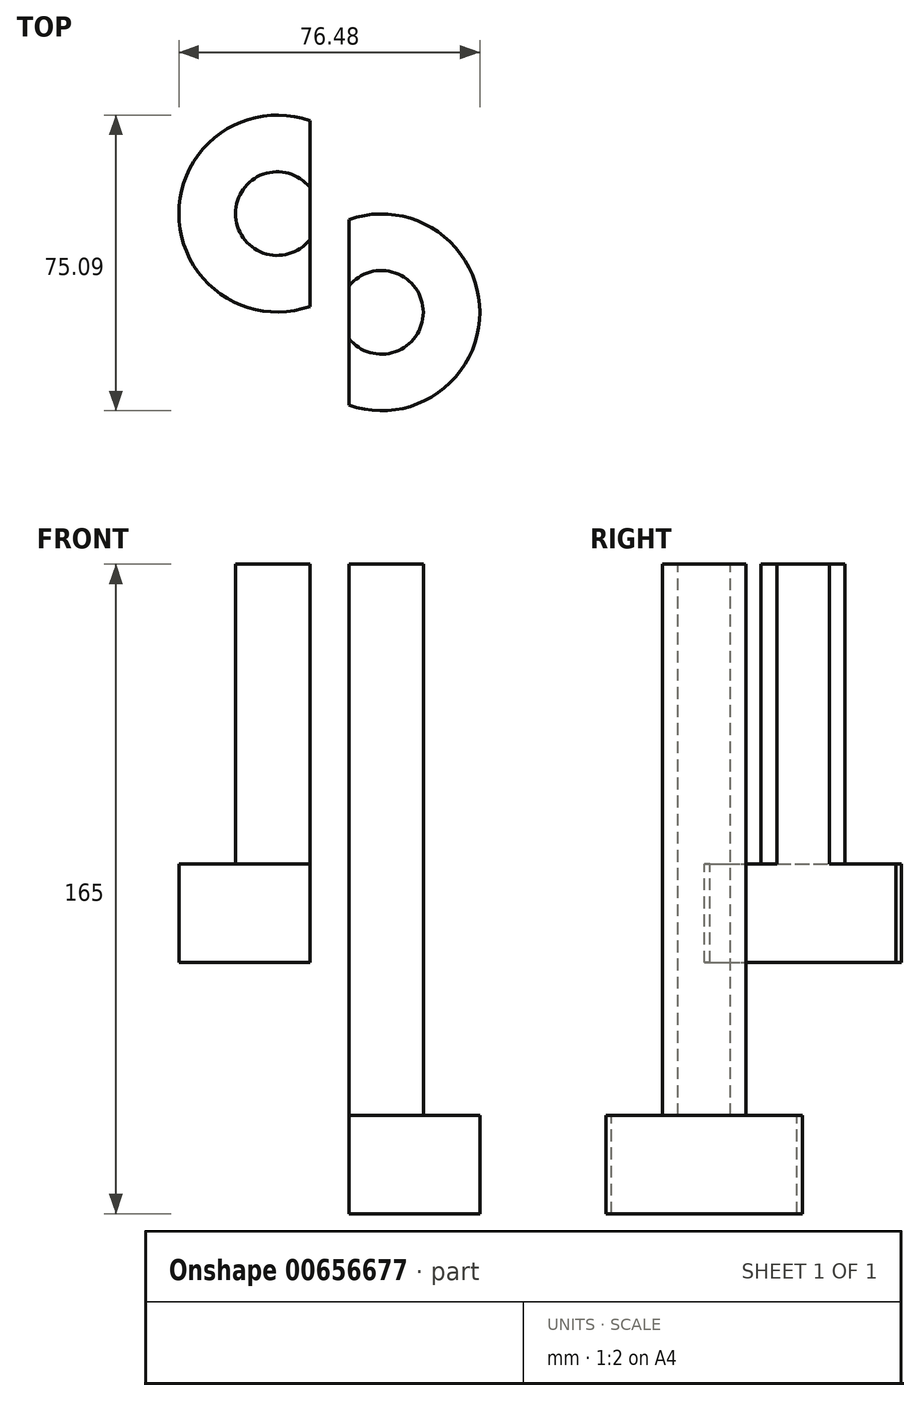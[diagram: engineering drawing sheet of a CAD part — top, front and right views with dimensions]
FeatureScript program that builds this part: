
annotation { "Feature Type Name" : "Feature", "Feature Type Description" : "" }
export const myFeature = defineFeature(function(context is Context, id is Id, definition is map)
    precondition{}
    {
        {
            var Q0;
            Q0=qCreatedBy(makeId("Top.planeOp"),FACE);
            var sketch = newSketch(context, id + "F0", { "sketchPlane" : qUnion([Q0])});
            skCircle(sketch, "E0", {"center": v(-17.72, 0) * mm, "radius": 10.62 * mm});
            skCircle(sketch, "E1", {"center": v(20.06, 0) * mm, "radius": 10.62 * mm});
            skLineSegment(sketch, "E2", {"start": v(-9.44, 6.66) * mm, "end": v(-9.44, -6.66) * mm});
            skLineSegment(sketch, "E3", {"start": v(11.78, 6.66) * mm, "end": v(11.78, -6.66) * mm});
            skPoint(sketch, "E4", {"position": v(-9.44, 0) * mm});
            skSolve(sketch);
        }
        {
            var Q0;
            {var subQ0=sQuery(id+"F0.wireOp",EDGE,"E2");Q0=makeQuery(id+"F0.imprint","IMPRINT",FACE,{"disambiguationData":[TD([[makeQuery(id+"F0.imprint","IMPRINT",EDGE,{"derivedFrom":subQ0}),-1.0]])]});}
            extrude(context, id + "F1", {"entities" : qUnion([Q0]), "depth" : 140 * mm, "offsetDistance" : 25 * mm});
        }
        {
            var Q0;
            {var subQ0=sQuery(id+"F0.wireOp",EDGE,"E3");Q0=makeQuery(id+"F0.imprint","IMPRINT",FACE,{"disambiguationData":[TD([[makeQuery(id+"F0.imprint","IMPRINT",EDGE,{"derivedFrom":subQ0}),1.0]])]});}
            extrude(context, id + "F2", {"entities" : qUnion([Q0]), "depth" : 76.2 * mm, "offsetDistance" : 25 * mm});
        }
        {
            var Q0;
            Q0=makeQuery(id+"F2.opExtrude","CAP_FACE",FACE,{"disambiguationData":[OSD([sQuery(id+"F0.wireOp",EDGE,"E1"),sQuery(id+"F0.wireOp",EDGE,"E3")])],"isStart":false});
            var sketch = newSketch(context, id + "F3", { "sketchPlane" : qUnion([Q0])});
            skLineSegment(sketch, "E5", {"start": v(11.78, -23.6) * mm, "end": v(11.78, 23.6) * mm});
            skArc(sketch, "E6", {"start": v(11.78, -23.6) * mm, "mid": v(45.06, 0) * mm, "end": v(11.78, 23.6) * mm});
            skSolve(sketch);
        }
        {
            var Q0;
            Q0 = qSketchRegion(id + "F3", true);
            extrude(context, id + "F4", {"entities" : qUnion([Q0]), "operationType" : NewBodyOperationType.ADD, "depth" : 25 * mm, "offsetDistance" : 25 * mm});
        }
        {
            var Q0;
            Q0=makeQuery(id+"F1.opExtrude","CAP_FACE",FACE,{"disambiguationData":[OSD([sQuery(id+"F0.wireOp",EDGE,"E0"),sQuery(id+"F0.wireOp",EDGE,"E2")])],"isStart":false});
            var sketch = newSketch(context, id + "F5", { "sketchPlane" : qUnion([Q0])});
            skLineSegment(sketch, "E7", {"start": v(-9.44, -23.6) * mm, "end": v(-9.44, 23.6) * mm});
            skArc(sketch, "E8", {"start": v(-9.44, 23.6) * mm, "mid": v(-42.72, 0) * mm, "end": v(-9.44, -23.6) * mm});
            skSolve(sketch);
        }
        {
            var Q0;
            Q0 = qSketchRegion(id + "F5", true);
            extrude(context, id + "F6", {"entities" : qUnion([Q0]), "operationType" : NewBodyOperationType.ADD, "depth" : 25 * mm, "offsetDistance" : 25 * mm});
        }
        {
            var Q0;
            Q0=makeQuery(id+"F1.opExtrude","SWEPT_BODY",BODY,{"disambiguationData":[OSD([sQuery(id+"F0.wireOp",EDGE,"E0"),sQuery(id+"F0.wireOp",EDGE,"E2")])]});
            var Q1;
            Q1=sQuery(id+"F0.wireOp",EDGE,"E2");
            transform(context, id + "F7", {"entities" : qUnion([Q0]), "transformType" : TransformType.ROTATION, "transformAxis" : qUnion([Q1]), "angle" : 180 * degree, "makeCopy" : false});
        }
        {
            var Q0;
            Q0=makeQuery(id+"F1.opExtrude","SWEPT_BODY",BODY,{"disambiguationData":[OSD([sQuery(id+"F0.wireOp",EDGE,"E0"),sQuery(id+"F0.wireOp",EDGE,"E2")])]});
            var Q1;
            Q1=sQuery(id+"F0.wireOp",VERTEX,"E0.center");
            var Q2;
            Q2=sQuery(id+"F0.wireOp",VERTEX,"E2.end");
            transform(context, id + "F8", {"entities" : qUnion([Q0]), "transformType" : TransformType.TRANSLATION_DISTANCE, "transformDirection" : qUnion([Q1, Q2]), "distance" : 40 * mm, "makeCopy" : false});
        }
        {
            var Q0;
            Q0=makeQuery(id+"F2.opExtrude","SWEPT_BODY",BODY,{"disambiguationData":[OSD([sQuery(id+"F0.wireOp",EDGE,"E1"),sQuery(id+"F0.wireOp",EDGE,"E3")])]});
            var Q1;
            Q1=makeQuery(id+"F2.opExtrude","CAP_EDGE",EDGE,{"disambiguationData":[OSD([sQuery(id+"F0.wireOp",EDGE,"E3")])],"isStart":true});
            transform(context, id + "F9", {"entities" : qUnion([Q0]), "transformType" : TransformType.ROTATION, "transformAxis" : qUnion([Q1]), "angle" : 180 * degree, "makeCopy" : false});
        }
    });
